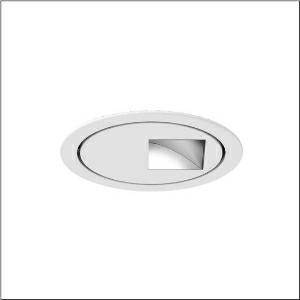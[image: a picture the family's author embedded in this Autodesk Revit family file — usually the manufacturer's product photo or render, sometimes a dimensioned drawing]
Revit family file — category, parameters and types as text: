
# Revit family: lunis_11_mini_round_51dk11b72wf21
name_source: partatom
category: Lighting Fixtures
units: mm (PartAtom-declared; Revit-internal decimal feet)

## family parameters
Cut with Voids When Loaded = No
Host = Face
Light Source = No
Part Type = Normal
Room Calculation Point = No
Round Connector Dimension = Use Diameter
Shared = No

## types (1)
- Lunis 11 mini round (1 x LED 3000K / CRI = 80 (unbekannt), 2380 lm, 3000K)
    Apparent Load = 28 VA
    CIE Flux Codes = 44 77 97 100 100
    Color Rendering = 80
    Color Temperature = 3000K
    Default Elevation = 1800 mm
    Description = Lunis 11 mini round, downlight, light control with wallwasher, of highly reflective aluminium, highly specular, light emission: direct distribution, LED rated luminous flux: 2.380lm, light colour: 830, control gear: ECG, with terminal, 3-pole, mains connection: 220..230V, AC/DC, 0/50..60Hz, LED module, luminaire module, of aluminium, highly specular, white, diameter: 176mm, clamping range: 1..40mm, recessing ring, of plastic, traffic white (RAL 9016), protection rating (complete): IP20, insulation class (complete): insulation class II (safety insulation), certification: CE, permissible ambient temperature for indoor applications: 0..+35°C, packaging unit: 1 piece
    Height = 0 mm  [stored 0 ft]
    Lamp = 1 x LED 3000K / CRI >= 80 (unbekannt)
    Lamp Light Flux = 2380 lm
    Lamp count = 1
    Length = 176 mm
    Luminous efficacy = 85 lm/W
    Manufacturer = Siteco
    ModVariant = No
    Model = 51DK11B72WF21
    Mounting Place = Ceiling
    Mounting Type = Recessed
    Number of Poles = 1
    OnlyDefault = Yes
    Power Factor = 1
    Product Name = Lunis 11 mini round
    Product group = downlight
    ProductGroupID = 400
    Protection Class = Protection class II
    Protection Degree = IP 20
    RLX_Detail_Level = 1
    RLX_Emergency_Light_Flux = 0 lm
    RLX_Emergency_Type = 0
    RLX_Emergency_Type_DB = No
    RlxData = <blob elided: 59405 chars, md5=e0a926dc>
    Socket = socket
    Standby Power = 0 W
    System Light Flux = 2380 lm
    System Power = 28 W
    Type Comments = Product without accessories
    Type Image = l_1004772.jpg
    URL = http://relux.com
    VarID = ---
    Voltage = 0 V
    Weight = 0.00 kg
    Width = 176 mm

note: [stored X ft] marks values corroborated as IEEE doubles in the binary element streams (Revit-internal decimal feet)

## geometry (parser evidence)
native form markers: Blend x4, Sweep x9
no freeform markers — native parametric forms only
